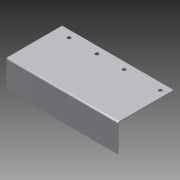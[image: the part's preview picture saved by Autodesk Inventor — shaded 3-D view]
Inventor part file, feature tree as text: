
AUTODESK INVENTOR PART (.ipt)
format: ipt  version: 2013 (Build 170138000, 138)  size: 109,056 bytes
history: native  units: in
note: dims shown in document units (in); Inventor stores cm internally (conversion verified against a paired STEP export)
features: sheet_metal_op x4, sketch x2, other x2
ambient origin geometry x8: Origin, YZ Plane, XZ Plane, XY Plane, X Axis, Y Axis, Z Axis, Center Point
bodies: Solid1 (feature_tree)
feature tree (8):
  sheet_metal_op  "Face1"
  sheet_metal_op  "Flange1"
  sketch  "Sketch1"  dims[d0=2.5984in]
  other  "Plate1"
  sketch  "Sketch2"  dims[d1=0.26in d2=0.26in d3=1.0in d4=1.75in d6=2.0in d7=2.0in d8=3.0in d9=8.0in d10=0.0625in d11=0.0625in d12=0.0312in d13=0.125in d14=0.0625in d15=2.0in d16=90.0deg d17=0.05in d18=0.25in d19=0.0625in d20=0.0625in]
  other  "Plate2"
  sheet_metal_op  "Bend1"
  sheet_metal_op  "Corner1"
